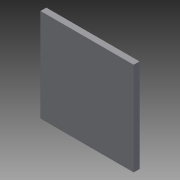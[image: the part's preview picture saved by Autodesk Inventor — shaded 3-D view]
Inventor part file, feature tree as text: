
AUTODESK INVENTOR PART (.ipt)
format: ipt  version: 2013 (Build 170138000, 138)  size: 138,752 bytes
history: native  units: mm
features: extrude x2, sketch x2, other x1
ambient origin geometry x8: Origin, YZ Plane, XZ Plane, XY Plane, X Axis, Y Axis, Z Axis, Center Point
feature tree (5):
  other  "ソリッド1"
  extrude  "押し出し1"  Depth=40.0mm
  extrude  "押し出し2"  Depth=40.0mm
  sketch  "スケッチ1"
  sketch  "スケッチ2"
